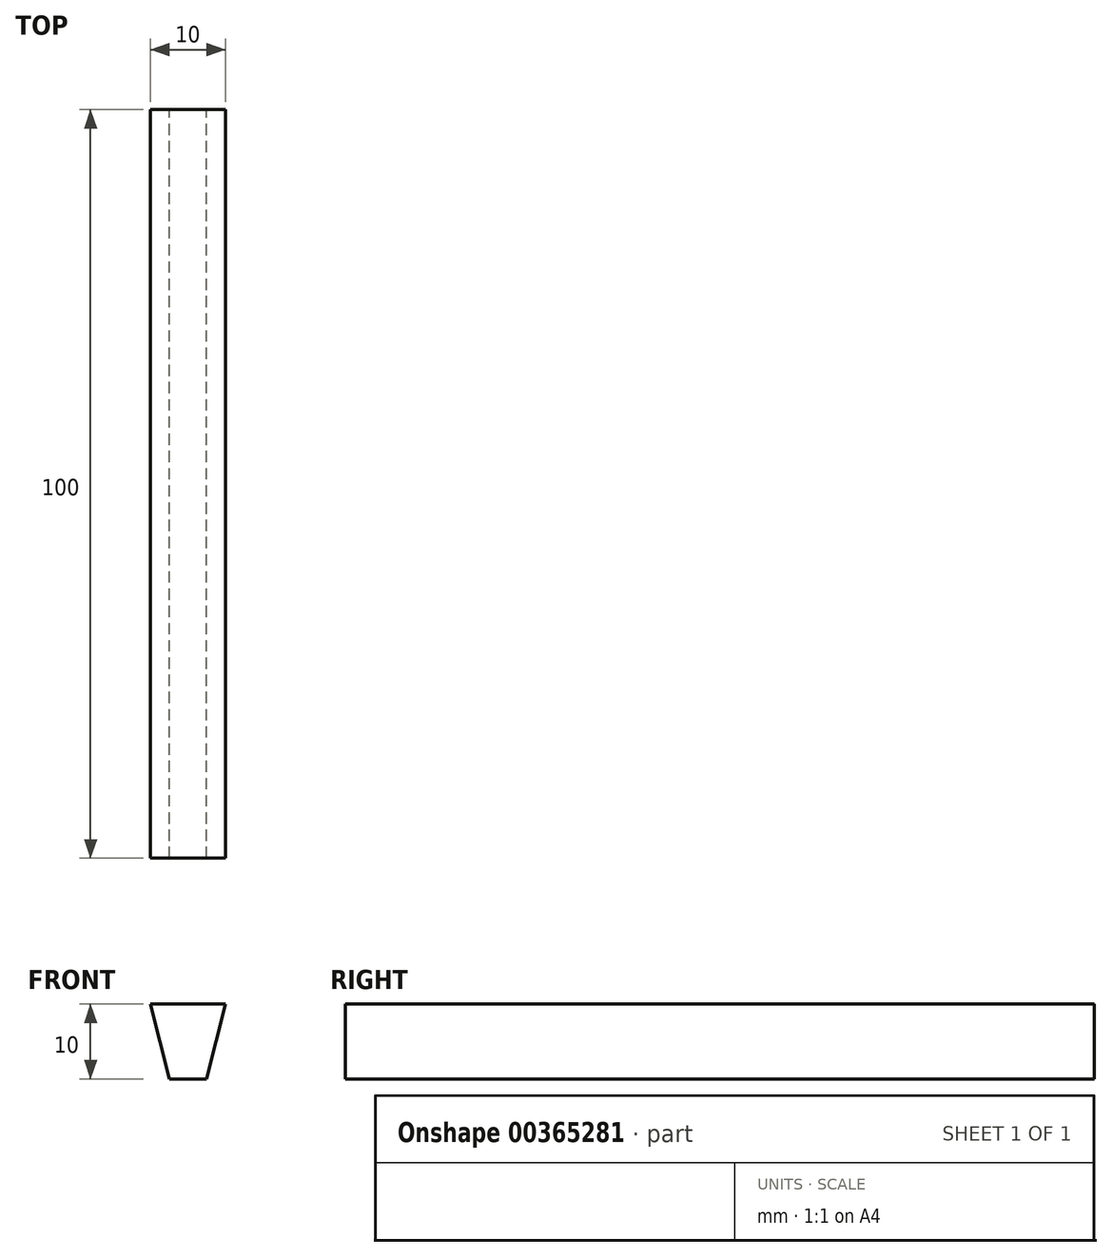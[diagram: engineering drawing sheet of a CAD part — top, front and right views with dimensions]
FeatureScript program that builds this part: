
annotation { "Feature Type Name" : "Feature", "Feature Type Description" : "" }
export const myFeature = defineFeature(function(context is Context, id is Id, definition is map)
    precondition{}
    {
        {
            var Q0;
            Q0=qCreatedBy(makeId("Front.planeOp"),FACE);
            var sketch = newSketch(context, id + "F0", { "sketchPlane" : qUnion([Q0])});
            skLineSegment(sketch, "E0", {"start": v(0, 0) * mm, "end": v(10, 0) * mm});
            skLineSegment(sketch, "E1", {"start": v(10, 0) * mm, "end": v(7.5, -10) * mm});
            skLineSegment(sketch, "E2", {"start": v(7.5, -10) * mm, "end": v(2.5, -10) * mm});
            skLineSegment(sketch, "E3", {"start": v(2.5, -10) * mm, "end": v(0, 0) * mm});
            skLineSegment(sketch, "E4", {"start": v(5, 0) * mm, "end": v(5, -10) * mm, "construction": true});
            skSolve(sketch);
        }
        {
            var Q0;
            Q0 = qSketchRegion(id + "F0", true);
            extrude(context, id + "F1", {"entities" : qUnion([Q0]), "depth" : 100 * mm});
        }
    });
